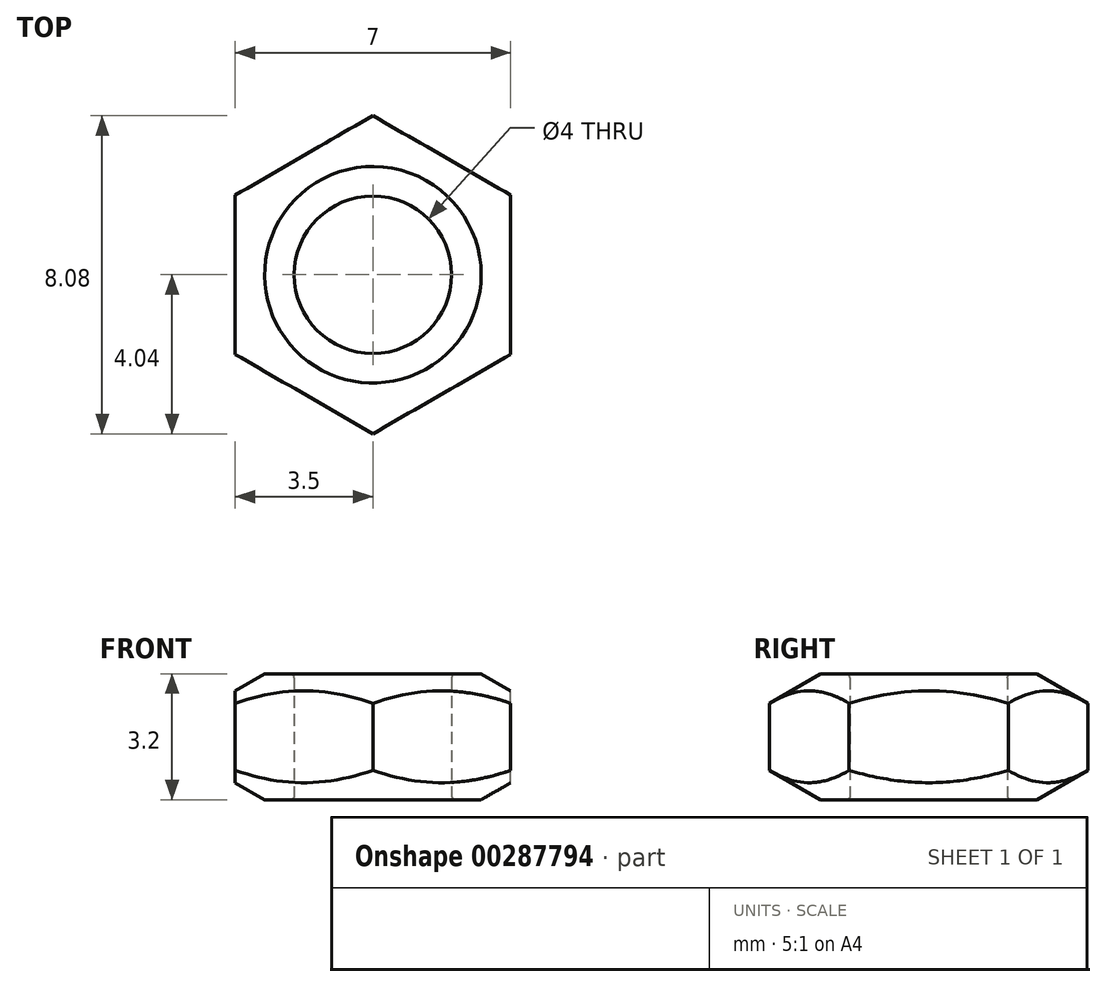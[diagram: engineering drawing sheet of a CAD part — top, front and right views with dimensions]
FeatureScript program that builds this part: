
annotation { "Feature Type Name" : "Feature", "Feature Type Description" : "" }
export const myFeature = defineFeature(function(context is Context, id is Id, definition is map)
    precondition{}
    {
        {
            var Q0;
            Q0=qCreatedBy(makeId("Top.planeOp"),FACE);
            var sketch = newSketch(context, id + "F0", { "sketchPlane" : qUnion([Q0])});
            skCircle(sketch, "E0.cCircle", {"center": v(0, 0) * mm, "radius": 3.5 * mm, "construction": true});
            skLineSegment(sketch, "E0.0", {"start": v(0, -4.04) * mm, "end": v(-3.5, -2.02) * mm});
            skLineSegment(sketch, "E0.1", {"start": v(-3.5, -2.02) * mm, "end": v(-3.5, 2.02) * mm});
            skLineSegment(sketch, "E0.2", {"start": v(-3.5, 2.02) * mm, "end": v(0, 4.04) * mm});
            skLineSegment(sketch, "E0.3", {"start": v(0, 4.04) * mm, "end": v(3.5, 2.02) * mm});
            skLineSegment(sketch, "E0.4", {"start": v(3.5, 2.02) * mm, "end": v(3.5, -2.02) * mm});
            skLineSegment(sketch, "E0.5", {"start": v(3.5, -2.02) * mm, "end": v(0, -4.04) * mm});
            skPoint(sketch, "E0.0.midPoint", {"position": v(-1.75, -3.03) * mm});
            skCircle(sketch, "E1", {"center": v(0, 0) * mm, "radius": 2 * mm});
            skSolve(sketch);
        }
        {
            var Q0;
            Q0=qSketchRegion(id+"F0",true);
            extrude(context, id + "F1", {"entities" : qUnion([Q0]), "depth" : 3.2 * mm});
        }
        {
            var Q0;
            Q0=qCreatedBy(makeId("Front.planeOp"),FACE);
            var sketch = newSketch(context, id + "F2", { "sketchPlane" : qUnion([Q0])});
            skLineSegment(sketch, "E2", {"start": v(0, 0) * mm, "end": v(0, 3.2) * mm, "construction": true});
            skLineSegment(sketch, "E3", {"start": v(0, 1.6) * mm, "end": v(3.5, 1.6) * mm, "construction": true});
            skLineSegment(sketch, "E4", {"start": v(3.5, 3.2) * mm, "end": v(5.36, 3.2) * mm});
            skLineSegment(sketch, "E5", {"start": v(5.36, 3.2) * mm, "end": v(5.36, 2.12) * mm});
            skLineSegment(sketch, "E6", {"start": v(5.36, 2.12) * mm, "end": v(3.5, 3.2) * mm});
            skLineSegment(sketch, "E7.MirrorCS", {"start": v(4.61, 3.2) * mm, "end": v(4.61, 2.12) * mm});
            skLineSegment(sketch, "E8.MirrorCS", {"start": v(4.61, 2.12) * mm, "end": v(2.75, 3.2) * mm});
            skLineSegment(sketch, "E9.MirrorCS", {"start": v(2.75, 3.2) * mm, "end": v(4.61, 3.2) * mm});
            skLineSegment(sketch, "E10.MirrorCS", {"start": v(3.5, 0) * mm, "end": v(5.36, 0) * mm});
            skLineSegment(sketch, "E11.MirrorCS", {"start": v(5.36, 0) * mm, "end": v(5.36, 1.08) * mm});
            skLineSegment(sketch, "E12.MirrorCS", {"start": v(5.36, 1.08) * mm, "end": v(3.5, 0) * mm});
            skLineSegment(sketch, "E13.MirrorCS", {"start": v(4.61, 0) * mm, "end": v(4.61, 1.08) * mm});
            skLineSegment(sketch, "E14.MirrorCS", {"start": v(2.75, 0) * mm, "end": v(4.61, 0) * mm});
            skLineSegment(sketch, "E15.MirrorCS", {"start": v(4.61, 1.08) * mm, "end": v(2.75, 0) * mm});
            skSolve(sketch);
        }
        {
            var Q0;
            Q0=qSketchRegion(id+"F2",true);
            var Q1;
            Q1=sQuery(id+"F2.wireOp",EDGE,"E2");
            revolve(context, id + "F3", {"operationType" : NewBodyOperationType.REMOVE, "entities" : qUnion([Q0]), "axis" : qUnion([Q1]), "revolveType" : RevolveType.FULL, "oppositeDirection" : true});
        }
        {
            var Q0;
            Q0=makeQuery(id+"F1.opExtrude","CAP_EDGE",EDGE,{"disambiguationData":[OSD([sQuery(id+"F0.wireOp",EDGE,"E1")])],"isStart":false});
            fillet(context, id + "F4", {"entities" : qUnion([Q0]), "radius" : .1 * mm, "tangentPropagation" : true, "allowEdgeOverflow" : false});
        }
        {
            var Q0;
            Q0=makeQuery(id+"F1.opExtrude","CAP_EDGE",EDGE,{"disambiguationData":[OSD([sQuery(id+"F0.wireOp",EDGE,"E1")])],"isStart":true});
            fillet(context, id + "F5", {"entities" : qUnion([Q0]), "radius" : .1 * mm, "tangentPropagation" : true, "allowEdgeOverflow" : false});
        }
    });
